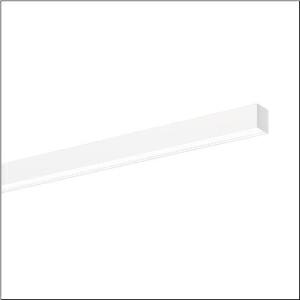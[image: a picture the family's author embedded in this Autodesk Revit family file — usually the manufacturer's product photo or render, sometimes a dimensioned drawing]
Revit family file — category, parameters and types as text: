
# Revit family: silica_r__21_51mx23da34wb_c22c
name_source: partatom
category: Lighting Fixtures
units: mm (PartAtom-declared; Revit-internal decimal feet)

## family parameters
Cut with Voids When Loaded = No
Host = Face
Light Source = No
Part Type = Normal
Room Calculation Point = No
Round Connector Dimension = Use Diameter
Shared = No

## types (1)
- --- (1 x LED, 3280 lm, 24.1 W, 3000K)
    Apparent Load = 24 VA
    CIE Flux Codes = 78 96 99 100 100
    Color Rendering = 80
    Color Temperature = 3000K
    Default Elevation = 1800 mm
    Description = Silica® 21, office luminaire, primary optical cover: prismatic diffuser, of PMMA, CAT 2 (L<= 3000cd/m²), light emission: direct distribution, primary light characteristic: symmetric, installation type: surface-mounted, LED, rated luminous flux: 3.280lm, luminous efficacy: 136lm/W, light colour: 830, colour temperature: 3000K, with terminal, 3+2-pole, max. 2.5mm², mains connection: 220..240V, AC, 50/60Hz, rated input power: 24.1W, luminaire housing, of aluminium, traffic white (RAL 9016), length: 1.204mm, width: 53mm, height: 53mm, protection rating (complete): IP20, insulation class (complete): insulation class I (protective earthing), certification: CE, permissible operating ambient temperature: 0..+35°C, standard: EN 50419, packaging unit: 1 piece
    Height = 0 mm  [stored 0 ft]
    Lamp = 1 x LED
    Lamp Light Flux = 3280 lm
    Lamp Power = 24.1 W
    Lamp count = 1
    Length = 1204 mm
    Luminous efficacy = 136 lm/W
    Manufacturer = Siteco
    ModVariant = No
    Model = 51MX23DA34WB
    Mounting Place = Ceiling
    Mounting Type = Recessed
    Number of Poles = 1
    OnlyDefault = Yes
    Power Factor = 1
    Product Name = Silica® 21
    Product group = office luminaire | ceiling recessed
    ProductGroupID = 401
    Protection Class = Protection class I
    Protection Degree = IP 20
    RLX_Detail_Level = 1
    RLX_Emergency_Light_Flux = 0 lm
    RLX_Emergency_Type = 0
    RLX_Emergency_Type_DB = No
    RlxData = <blob elided: 18833 chars, md5=d74c2236>
    Socket = socket
    Standby Power = 0 W
    System Light Flux = 3280 lm
    System Power = 24 W
    Type Comments = factory setting: luminous flux: 100 % | dim-lin: 254 | 345 mA
    Type Image = l_1297777.jpg
    URL = http://relux.com
    VarID = @adj_050243
    Voltage = 0 V
    Weight = 0.00 kg
    Width = 53 mm

note: [stored X ft] marks values corroborated as IEEE doubles in the binary element streams (Revit-internal decimal feet)

## geometry (parser evidence)
native form markers: Blend x4, Sweep x11
no freeform markers — native parametric forms only
